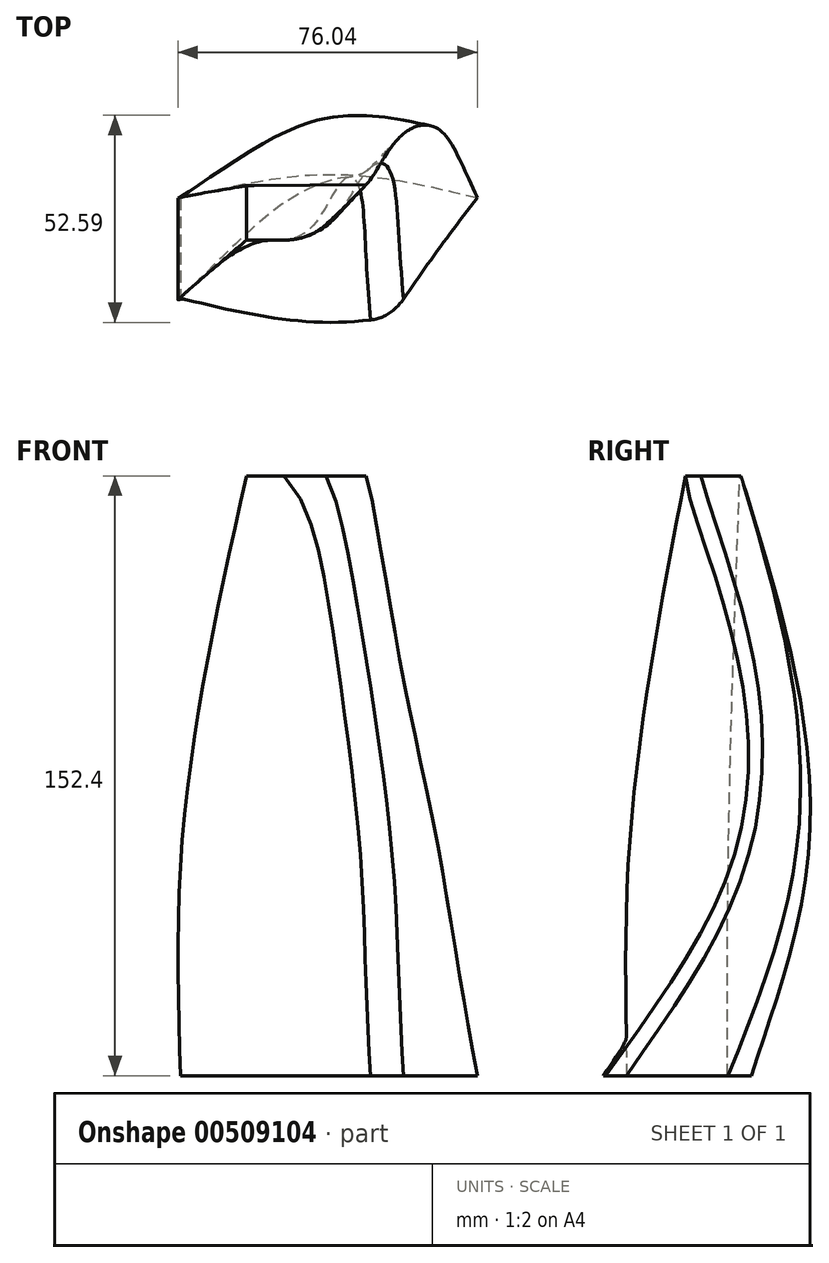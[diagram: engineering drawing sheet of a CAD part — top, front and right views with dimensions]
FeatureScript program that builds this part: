
annotation { "Feature Type Name" : "Feature", "Feature Type Description" : "" }
export const myFeature = defineFeature(function(context is Context, id is Id, definition is map)
    precondition{}
    {
        {
            var Q0;
            Q0=qCreatedBy(makeId("Top.planeOp"),FACE);
            cPlane(context, id + "F0", {"entities" : qUnion([Q0]), "cplaneType" : CPlaneType.OFFSET, "offset" : 50.8 * mm, "width" : 152.4 * mm, "height" : 152.4 * mm});
        }
        {
            var Q0;
            Q0=qCreatedBy(id+"F0.planeOp",FACE);
            cPlane(context, id + "F1", {"entities" : qUnion([Q0]), "cplaneType" : CPlaneType.OFFSET, "offset" : 101.6 * mm, "width" : 152.4 * mm, "height" : 152.4 * mm});
        }
        {
            var Q0;
            Q0=qCreatedBy(makeId("Top.planeOp"),FACE);
            var sketch = newSketch(context, id + "F2", { "sketchPlane" : qUnion([Q0])});
            skLineSegment(sketch, "E0", {"start": v(-38.1, 12.7) * mm, "end": v(-38.1, -12.7) * mm});
            skLineSegment(sketch, "E1", {"start": v(38.1, 12.7) * mm, "end": v(38.1, -12.7) * mm});
            skFitSpline(sketch, "E2", {"points": [v(-38.1, -12.7) * mm, v(0, -18.8) * mm, v(38.1, -12.7) * mm], "startDerivative": vector(76.2, -18.3) * mm, "endDerivative": vector(76.2, 18.3) * mm});
            skFitSpline(sketch, "E3.MirrorCS", {"points": [v(-38.1, 12.7) * mm, v(0, 18.8) * mm, v(38.1, 12.7) * mm], "startDerivative": vector(76.2, 18.3) * mm, "endDerivative": vector(76.2, -18.3) * mm});
            skSolve(sketch);
        }
        {
            var Q0;
            Q0=qCreatedBy(id+"F0.planeOp",FACE);
            var sketch = newSketch(context, id + "F3", { "sketchPlane" : qUnion([Q0])});
            skLineSegment(sketch, "E4", {"start": v(-38.26, 12.93) * mm, "end": v(-38.26, -12.6) * mm});
            skLineSegment(sketch, "E5", {"start": v(38.3, 9.95) * mm, "end": v(38.3, 27.39) * mm});
            skFitSpline(sketch, "E6", {"points": [v(-38.26, 12.93) * mm, v(0, 32.28) * mm, v(38.3, 27.39) * mm], "startDerivative": vector(73.23, 48.14) * mm, "endDerivative": vector(79.12, -13.46) * mm});
            skFitSpline(sketch, "E7", {"points": [v(-38.26, -12.6) * mm, v(0, 11.65) * mm, v(38.3, 9.95) * mm], "startDerivative": vector(71.69, 57.74) * mm, "endDerivative": vector(80.73, -7.23) * mm});
            skSolve(sketch);
        }
        {
            var Q0;
            Q0=qCreatedBy(id+"F1.planeOp",FACE);
            var sketch = newSketch(context, id + "F4", { "sketchPlane" : qUnion([Q0])});
            skLineSegment(sketch, "E8", {"start": v(-21.36, 15.94) * mm, "end": v(-21.36, 2.1) * mm});
            skLineSegment(sketch, "E9", {"start": v(-21.36, 2.1) * mm, "end": v(21.66, 2.1) * mm});
            skLineSegment(sketch, "E10", {"start": v(21.66, 2.1) * mm, "end": v(21.66, 16.29) * mm});
            skLineSegment(sketch, "E11", {"start": v(21.66, 16.29) * mm, "end": v(-21.36, 15.94) * mm});
            skSolve(sketch);
        }
        {
            var Q0;
            Q0=makeQuery(id+"F2.imprint","IMPRINT",FACE,{"disambiguationData":[TD([[makeQuery(id+"F2.imprint","IMPRINT",EDGE,{"derivedFrom":sQuery(id+"F2.wireOp",EDGE,"E0")}),1.0]])]});
            var Q1;
            Q1=makeQuery(id+"F3.imprint","IMPRINT",FACE,{"disambiguationData":[TD([[makeQuery(id+"F3.imprint","IMPRINT",EDGE,{"derivedFrom":sQuery(id+"F3.wireOp",EDGE,"E4")}),1.0]])]});
            var Q2;
            Q2=makeQuery(id+"F4.imprint","IMPRINT",FACE,{"disambiguationData":[TD([[makeQuery(id+"F4.imprint","IMPRINT",EDGE,{"derivedFrom":sQuery(id+"F4.wireOp",EDGE,"E8")}),1.0]])]});
            loft(context, id + "F5", {"sheetProfilesArray" : [{ "sheetProfileEntities" : qUnion([Q0]) }, { "sheetProfileEntities" : qUnion([Q1]) }, { "sheetProfileEntities" : qUnion([Q2]) }]});
        }
        {
            var Q0;
            Q0=makeQuery(id+"F5.opLoft","SWEPT_EDGE",EDGE,{"disambiguationData":[OSD([sQuery(id+"F3.wireOp",EDGE,"E5"),sQuery(id+"F3.wireOp",EDGE,"E7"),sQuery(id+"F4.wireOp",EDGE,"E9"),sQuery(id+"F4.wireOp",EDGE,"E10")])]});
            chamfer(context, id + "F6", {"entities" : qUnion([Q0]), "width" : 25.4 * mm, "tangentPropagation" : true});
        }
        {
            var Q0;
            {var subQ0=sQuery(id+"F3.wireOp",EDGE,"E7");var subQ1=sQuery(id+"F3.wireOp",EDGE,"E5");var subQ2=sQuery(id+"F2.wireOp",EDGE,"E2");var subQ3=sQuery(id+"F2.wireOp",EDGE,"E1");Q0=makeQuery(id+"F6.opChamfer","BLEND_EDGE",EDGE,{"blendedFrom":[makeQuery(id+"F5.opLoft","SWEPT_EDGE",EDGE,{"disambiguationData":[OSD([subQ3,subQ2,subQ1,subQ0])]}),makeQuery(id+"F5.opLoft","SWEPT_FACE",FACE,{"disambiguationData":[OSD([sQuery(id+"F2.wireOp",EDGE,"E0"),subQ3,subQ2,sQuery(id+"F3.wireOp",EDGE,"E4"),subQ1,subQ0])]})],"blendedInto":[makeQuery(id+"F5.opLoft","SWEPT_FACE",FACE,{"disambiguationData":[OSD([sQuery(id+"F2.wireOp",EDGE,"E0"),subQ3,subQ2,sQuery(id+"F3.wireOp",EDGE,"E4"),subQ1,subQ0])]})]});}
            fillet(context, id + "F7", {"entities" : qUnion([Q0]), "radius" : 12.7 * mm, "tangentPropagation" : true, "allowEdgeOverflow" : false});
        }
    });
